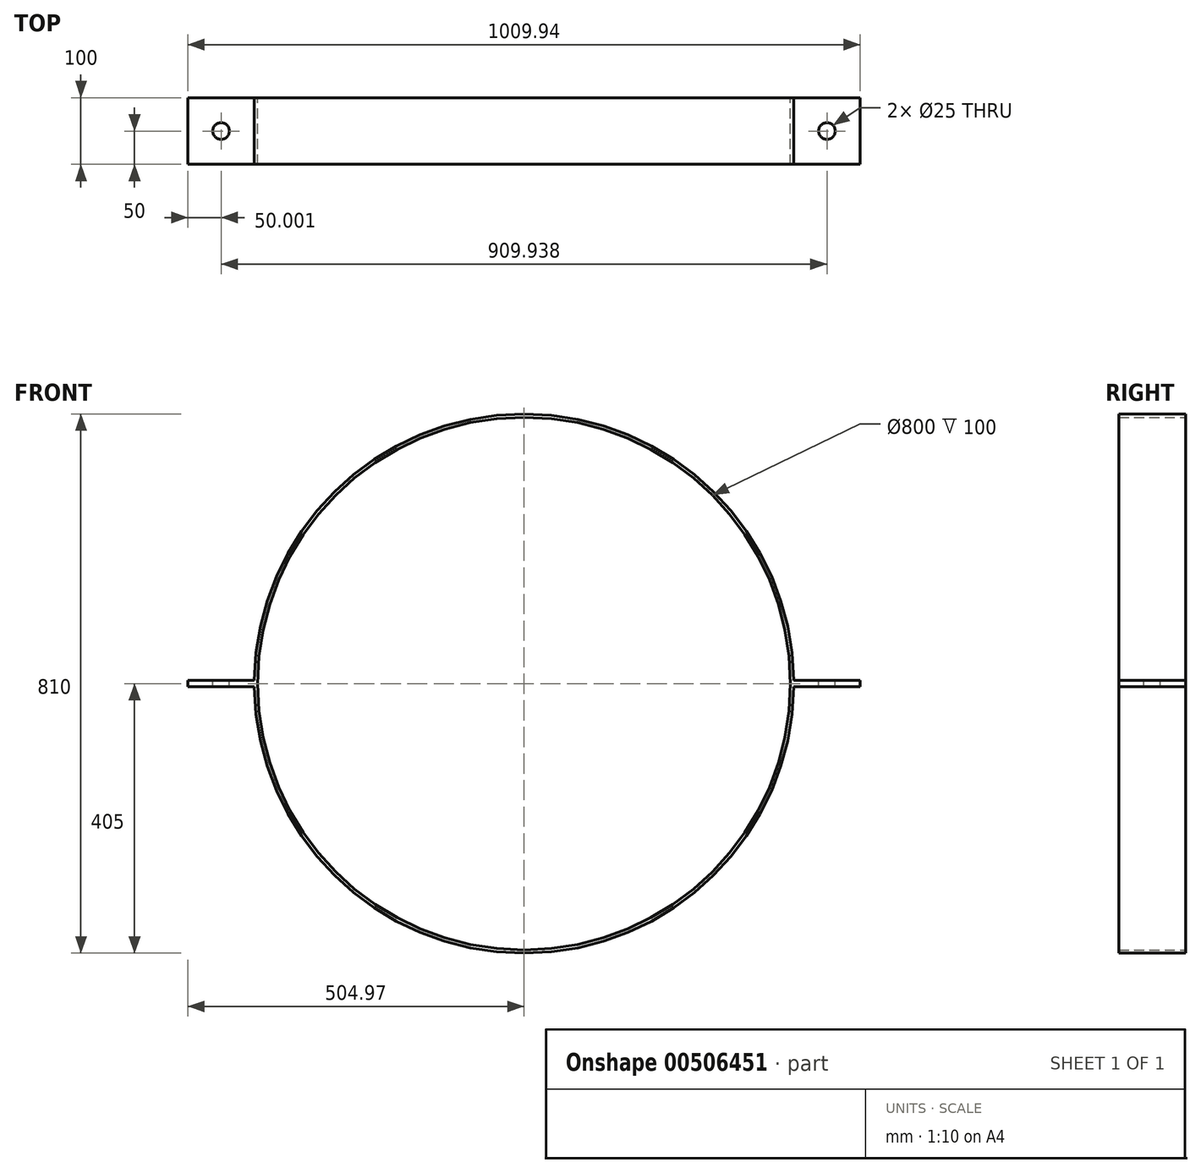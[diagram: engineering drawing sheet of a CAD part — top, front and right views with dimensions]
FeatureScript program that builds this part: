
annotation { "Feature Type Name" : "Feature", "Feature Type Description" : "" }
export const myFeature = defineFeature(function(context is Context, id is Id, definition is map)
    precondition{}
    {
        {
            var Q0;
            Q0=qCreatedBy(makeId("Front.planeOp"),FACE);
            var sketch = newSketch(context, id + "F0", { "sketchPlane" : qUnion([Q0])});
            skCircle(sketch, "E0", {"center": v(0, 0) * mm, "radius": 400 * mm});
            skCircle(sketch, "E1", {"center": v(0, 0) * mm, "radius": 405 * mm});
            skLineSegment(sketch, "E2", {"start": v(0, 0) * mm, "end": v(-690.21, 0) * mm, "construction": true});
            skLineSegment(sketch, "E3", {"start": v(-404.97, 5) * mm, "end": v(-504.97, 5) * mm});
            skLineSegment(sketch, "E4", {"start": v(-504.97, 5) * mm, "end": v(-504.97, 0) * mm});
            skLineSegment(sketch, "E5.MirrorCS", {"start": v(-404.97, -5) * mm, "end": v(-504.97, -5) * mm});
            skLineSegment(sketch, "E6.MirrorCS", {"start": v(-504.97, -5) * mm, "end": v(-504.97, 0) * mm});
            skLineSegment(sketch, "E7", {"start": v(0, 0) * mm, "end": v(0, 668.71) * mm, "construction": true});
            skLineSegment(sketch, "E8.MirrorCS", {"start": v(504.97, 5) * mm, "end": v(504.97, 0) * mm});
            skLineSegment(sketch, "E9.MirrorCS", {"start": v(504.97, -5) * mm, "end": v(504.97, 0) * mm});
            skLineSegment(sketch, "E10.MirrorCS", {"start": v(404.97, 5) * mm, "end": v(504.97, 5) * mm});
            skLineSegment(sketch, "E11.MirrorCS", {"start": v(404.97, -5) * mm, "end": v(504.97, -5) * mm});
            skSolve(sketch);
        }
        {
            var Q0;
            Q0=qSketchRegion(id+"F0",true);
            extrude(context, id + "F1", {"entities" : qUnion([Q0]), "depth" : 100 * mm});
        }
        {
            var Q0;
            Q0=makeQuery(id+"F1.opExtrude","SWEPT_FACE",FACE,{"disambiguationData":[OSD([sQuery(id+"F0.wireOp",EDGE,"E3")])]});
            var sketch = newSketch(context, id + "F2", { "sketchPlane" : qUnion([Q0])});
            skLineSegment(sketch, "E12", {"start": v(-454.97, 0) * mm, "end": v(-454.97, -100) * mm, "construction": true});
            skLineSegment(sketch, "E13", {"start": v(-504.97, -50) * mm, "end": v(-404.97, -50) * mm, "construction": true});
            skCircle(sketch, "E14", {"center": v(-454.97, -50) * mm, "radius": 12.5 * mm});
            skCircle(sketch, "E15.MirrorC", {"center": v(454.97, -50) * mm, "radius": 12.5 * mm});
            skSolve(sketch);
        }
        {
            var Q0;
            Q0=qSketchRegion(id+"F2",true);
            extrude(context, id + "F3", {"entities" : qUnion([Q0]), "operationType" : NewBodyOperationType.REMOVE, "oppositeDirection" : true, "depth" : 25 * mm});
        }
    });
